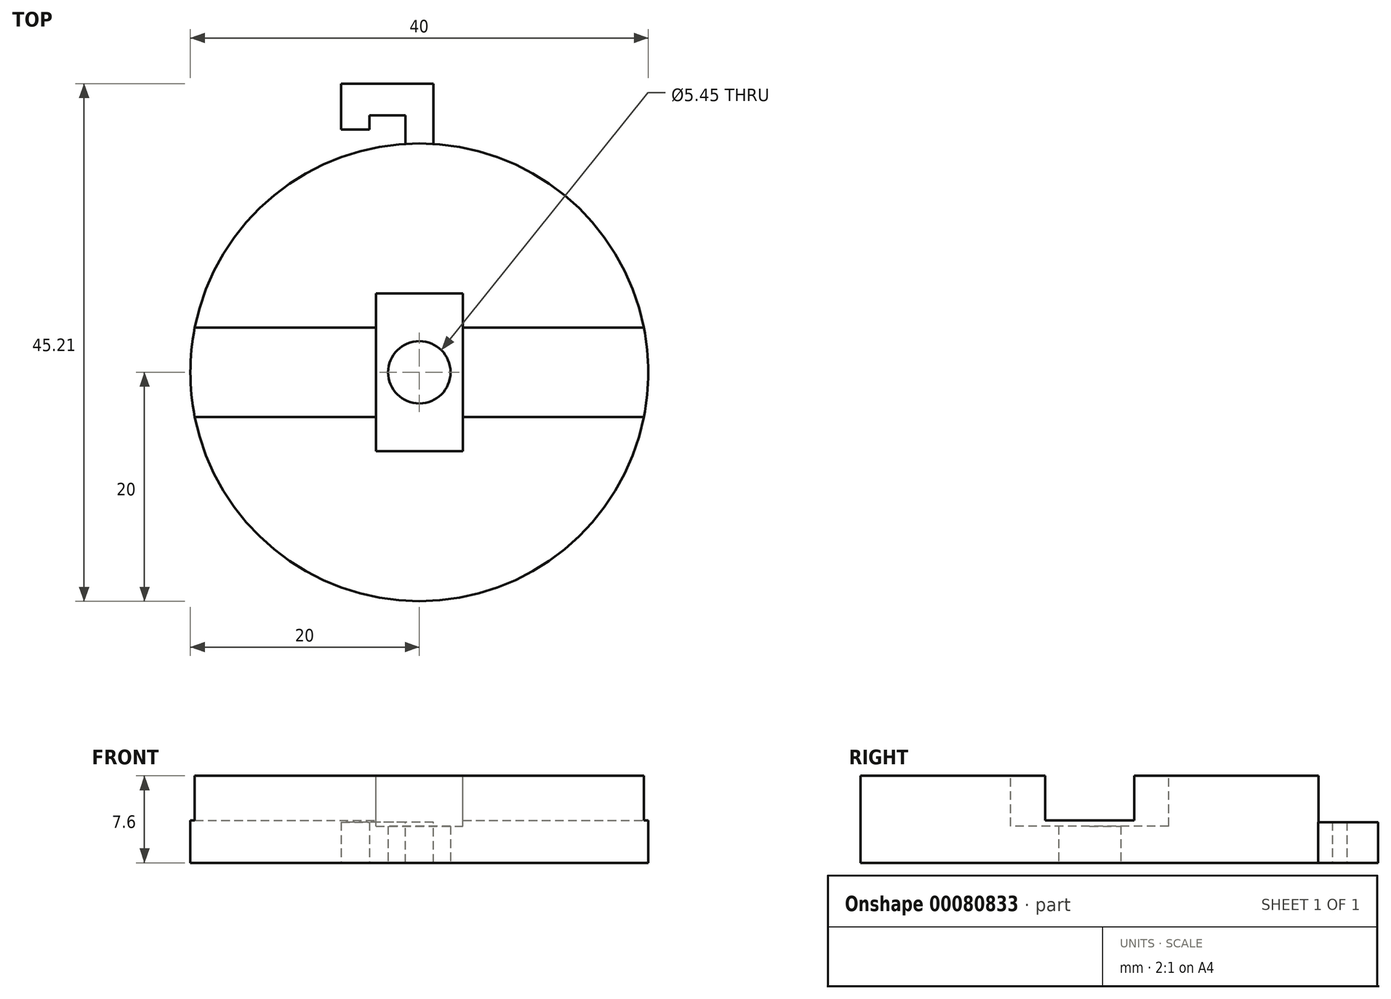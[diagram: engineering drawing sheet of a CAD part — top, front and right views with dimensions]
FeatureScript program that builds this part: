
annotation { "Feature Type Name" : "Feature", "Feature Type Description" : "" }
export const myFeature = defineFeature(function(context is Context, id is Id, definition is map)
    precondition{}
    {
        {
            var Q0;
            Q0=qCreatedBy(makeId("Top.planeOp"),FACE);
            var sketch = newSketch(context, id + "F0", { "sketchPlane" : qUnion([Q0])});
            skCircle(sketch, "E0", {"center": v(0, 0) * mm, "radius": 20 * mm});
            skSolve(sketch);
        }
        {
            var Q0;
            Q0 = qSketchRegion(id + "F0", true);
            extrude(context, id + "F1", {"entities" : qUnion([Q0]), "oppositeDirection" : true, "depth" : 7.6 * mm});
        }
        {
            var Q0;
            Q0=makeQuery(id+"F1.opExtrude","CAP_FACE",FACE,{"disambiguationData":[OSD([sQuery(id+"F0.wireOp",EDGE,"E0")])],"isStart":true});
            var sketch = newSketch(context, id + "F2", { "sketchPlane" : qUnion([Q0])});
            skLineSegment(sketch, "E1", {"start": v(-19.62, 3.9) * mm, "end": v(19.62, 3.9) * mm});
            skLineSegment(sketch, "E2", {"start": v(-19.62, -3.9) * mm, "end": v(19.62, -3.9) * mm});
            skSolve(sketch);
        }
        {
            var Q0;
            {var subQ0=sQuery(id+"F2.wireOp",EDGE,"E1");Q0=makeQuery(id+"F2.imprint","IMPRINT",FACE,{"disambiguationData":[TD([[makeQuery(id+"F2.imprint","IMPRINT",EDGE,{"derivedFrom":subQ0}),-1.0]])]});}
            extrude(context, id + "F3", {"entities" : qUnion([Q0]), "operationType" : NewBodyOperationType.REMOVE, "oppositeDirection" : true, "depth" : 3.9 * mm});
        }
        {
            var Q0;
            {var subQ0=sQuery(id+"F0.wireOp",EDGE,"E0");Q0=makeQuery(id+"F3.boolean.opBoolean","SPLIT",FACE,{"disambiguationData":[TD([makeQuery(id+"F3.opExtrude","SWEPT_FACE",FACE,{"disambiguationData":[OSD([sQuery(id+"F2.wireOp",EDGE,"E2")])]})])],"derivedFrom":makeQuery(id+"F1.opExtrude","CAP_FACE",FACE,{"disambiguationData":[OSD([subQ0])],"isStart":true})});}
            var sketch = newSketch(context, id + "F4", { "sketchPlane" : qUnion([Q0])});
            skLineSegment(sketch, "E3.bottom", {"start": v(-3.8, -3.9) * mm, "end": v(3.8, -3.9) * mm});
            skLineSegment(sketch, "E3.top", {"start": v(-3.8, -6.9) * mm, "end": v(3.8, -6.9) * mm});
            skLineSegment(sketch, "E3.left", {"start": v(-3.8, -3.9) * mm, "end": v(-3.8, -6.9) * mm});
            skLineSegment(sketch, "E3.right", {"start": v(3.8, -3.9) * mm, "end": v(3.8, -6.9) * mm});
            skSolve(sketch);
        }
        {
            var Q0;
            {var subQ0=sQuery(id+"F0.wireOp",EDGE,"E0");Q0=makeQuery(id+"F3.boolean.opBoolean","SPLIT",FACE,{"disambiguationData":[TD([makeQuery(id+"F3.opExtrude","SWEPT_FACE",FACE,{"disambiguationData":[OSD([sQuery(id+"F2.wireOp",EDGE,"E1")])]})])],"derivedFrom":makeQuery(id+"F1.opExtrude","CAP_FACE",FACE,{"disambiguationData":[OSD([subQ0])],"isStart":true})});}
            var sketch = newSketch(context, id + "F5", { "sketchPlane" : qUnion([Q0])});
            skLineSegment(sketch, "E4.bottom", {"start": v(-3.8, 3.9) * mm, "end": v(3.8, 3.9) * mm});
            skLineSegment(sketch, "E4.top", {"start": v(-3.8, 6.9) * mm, "end": v(3.8, 6.9) * mm});
            skLineSegment(sketch, "E4.left", {"start": v(-3.8, 3.9) * mm, "end": v(-3.8, 6.9) * mm});
            skLineSegment(sketch, "E4.right", {"start": v(3.8, 3.9) * mm, "end": v(3.8, 6.9) * mm});
            skSolve(sketch);
        }
        {
            var Q0;
            Q0 = qSketchRegion(id + "F4", true);
            var Q1;
            Q1 = qSketchRegion(id + "F5", true);
            extrude(context, id + "F6", {"entities" : qUnion([Q0, Q1]), "operationType" : NewBodyOperationType.REMOVE, "oppositeDirection" : true, "depth" : 4.4 * mm});
        }
        {
            var Q0;
            Q0=makeQuery(id+"F3.boolean.opBoolean","COPY",FACE,{"derivedFrom":makeQuery(id+"F3.opExtrude","CAP_FACE",FACE,{"disambiguationData":[OSD([sQuery(id+"F0.wireOp",EDGE,"E0"),sQuery(id+"F2.wireOp",EDGE,"E1"),sQuery(id+"F2.wireOp",EDGE,"E2")])],"isStart":false})});
            var sketch = newSketch(context, id + "F7", { "sketchPlane" : qUnion([Q0])});
            skLineSegment(sketch, "E5.bottom", {"start": v(-3.8, 3.9) * mm, "end": v(3.8, 3.9) * mm});
            skLineSegment(sketch, "E5.top", {"start": v(-3.8, -3.9) * mm, "end": v(3.8, -3.9) * mm});
            skLineSegment(sketch, "E5.left", {"start": v(-3.8, 3.9) * mm, "end": v(-3.8, -3.9) * mm});
            skLineSegment(sketch, "E5.right", {"start": v(3.8, 3.9) * mm, "end": v(3.8, -3.9) * mm});
            skSolve(sketch);
        }
        {
            var Q0;
            Q0 = qSketchRegion(id + "F7", true);
            extrude(context, id + "F8", {"entities" : qUnion([Q0]), "operationType" : NewBodyOperationType.REMOVE, "oppositeDirection" : true, "depth" : .5 * mm});
        }
        {
            var Q0;
            Q0=qCreatedBy(makeId("Top.planeOp"),FACE);
            cPlane(context, id + "F9", {"entities" : qUnion([Q0]), "cplaneType" : CPlaneType.OFFSET, "offset" : 7.6 * mm, "oppositeDirection" : true, "width" : 150 * mm, "height" : 150 * mm});
        }
        {
            var Q0;
            Q0=qCreatedBy(id+"F9.planeOp",FACE);
            var sketch = newSketch(context, id + "F10", { "sketchPlane" : qUnion([Q0])});
            skLineSegment(sketch, "E6", {"start": v(1.23, 19.96) * mm, "end": v(1.23, 25.21) * mm});
            skLineSegment(sketch, "E7", {"start": v(-1.23, 19.96) * mm, "end": v(-1.23, 22.46) * mm});
            skLineSegment(sketch, "E8", {"start": v(1.23, 25.21) * mm, "end": v(-6.83, 25.21) * mm});
            skLineSegment(sketch, "E9", {"start": v(-6.83, 25.21) * mm, "end": v(-6.83, 21.21) * mm});
            skLineSegment(sketch, "E10", {"start": v(-6.83, 21.21) * mm, "end": v(-4.38, 21.21) * mm});
            skLineSegment(sketch, "E11", {"start": v(-1.23, 22.46) * mm, "end": v(-4.38, 22.46) * mm});
            skLineSegment(sketch, "E12", {"start": v(-4.38, 21.21) * mm, "end": v(-4.38, 22.46) * mm});
            skLineSegment(sketch, "E13", {"start": v(1.23, 19.96) * mm, "end": v(1.23, 19.84) * mm});
            skLineSegment(sketch, "E14", {"start": v(1.23, 19.84) * mm, "end": v(-1.23, 19.8) * mm});
            skLineSegment(sketch, "E15", {"start": v(-1.23, 19.8) * mm, "end": v(-1.23, 19.96) * mm});
            skSolve(sketch);
        }
        {
            var Q0;
            Q0 = qSketchRegion(id + "F10", true);
            extrude(context, id + "F11", {"entities" : qUnion([Q0]), "operationType" : NewBodyOperationType.ADD, "depth" : 3.55 * mm});
        }
        {
            var Q0;
            Q0=makeQuery(id+"F11.boolean.opBoolean","MERGE",FACE,{"derivedFrom":[makeQuery(id+"F1.opExtrude","CAP_FACE",FACE,{"disambiguationData":[OSD([sQuery(id+"F0.wireOp",EDGE,"E0")])],"isStart":false}),makeQuery(id+"F11.opExtrude","CAP_FACE",FACE,{"disambiguationData":[OSD([sQuery(id+"F10.wireOp",EDGE,"E6"),sQuery(id+"F10.wireOp",EDGE,"E7"),sQuery(id+"F10.wireOp",EDGE,"E8"),sQuery(id+"F10.wireOp",EDGE,"E9"),sQuery(id+"F10.wireOp",EDGE,"E10"),sQuery(id+"F10.wireOp",EDGE,"E11"),sQuery(id+"F10.wireOp",EDGE,"E12"),sQuery(id+"F10.wireOp",EDGE,"E13"),sQuery(id+"F10.wireOp",EDGE,"E14"),sQuery(id+"F10.wireOp",EDGE,"E15")])],"isStart":true})]});
            var sketch = newSketch(context, id + "F12", { "sketchPlane" : qUnion([Q0])});
            skCircle(sketch, "E16", {"center": v(0, 0) * mm, "radius": 2.73 * mm});
            skSolve(sketch);
        }
        {
            var Q0;
            Q0 = qSketchRegion(id + "F12", true);
            extrude(context, id + "F13", {"entities" : qUnion([Q0]), "operationType" : NewBodyOperationType.REMOVE, "oppositeDirection" : true, "depth" : 7.6 * mm});
        }
    });
